# Revit family: Plumbing_Joints_Aignep_Ball-Valve-Male-Female-Inox316L-66069
name_source: partatom
category: Pipe Accessories
revit_build: Autodesk Revit 2018 (Build: 20170223_1515(x64)
units: mm (PartAtom-declared; Revit-internal decimal feet)

## family parameters
Always vertical = Yes
Cut with Voids When Loaded = No
OmniClass Number = 23.27.43.00
OmniClass Title = Pipe Fittings
Part Type = Valve - Breaks Into
Round Connector Dimension = Use Diameter
Shared = No
Work Plane-Based = No

## types (1)
- 1/2"
    A = 12.7 mm  [stored 0.0416667 ft]
    Assembly Code = D2040100
    B = 12.7 mm  [stored 0.0416667 ft]
    BIMobject category = Valves
    CH = 26.5 mm
    Description = Ball valve male ga iso 228 - female g iso 228 - INOX316L
    Design country = Italy
    Edition number = 1
    G = 110 mm  [stored 0.360892 ft]
    H = 55 mm  [stored 0.180446 ft]
    IFC Classification = Pipe Fitting
    Keynote = 15410
    L = 65 mm
    Manufacturer = Aignep Spa
    Manufacturer country = Italy
    Manufacturer name = Aignep Spa
    Model = 66069
    Nominal Diameter = 12.700 mm
    OmniClass Code = 23-27 43 00
    OmniClass Description = Pipe Fittings
    Product Guid = 9cf7bb1f-fcd4-4dd5-8af6-e56d9f783844
    Product Material = AIGNEP - Inox - Grey
    Product SKU = Ball-Valve-Male-Ga-Iso-228-Female-G-Iso-228-Inox316L-66069
    Product certification = https://www.aignep.com
    Product data url = https://www.bimobject.com
    Product family = INFINITY
    Product group = Valves
    Product name = Ball Valve Male Ga Iso 228 - Female G Iso 228 - Inox316L - 66069
    Product url = https://www.aignep.com
    QR code = https://www.bimobject.com
    Tick Size = 10.16 mm  [stored 0.0333333 ft]
    URL = https://www.aignep.com

note: [stored X ft] marks values corroborated as IEEE doubles in the binary element streams (Revit-internal decimal feet)

## geometry (parser evidence)
native form markers: Sweep x1
no freeform markers — native parametric forms only
